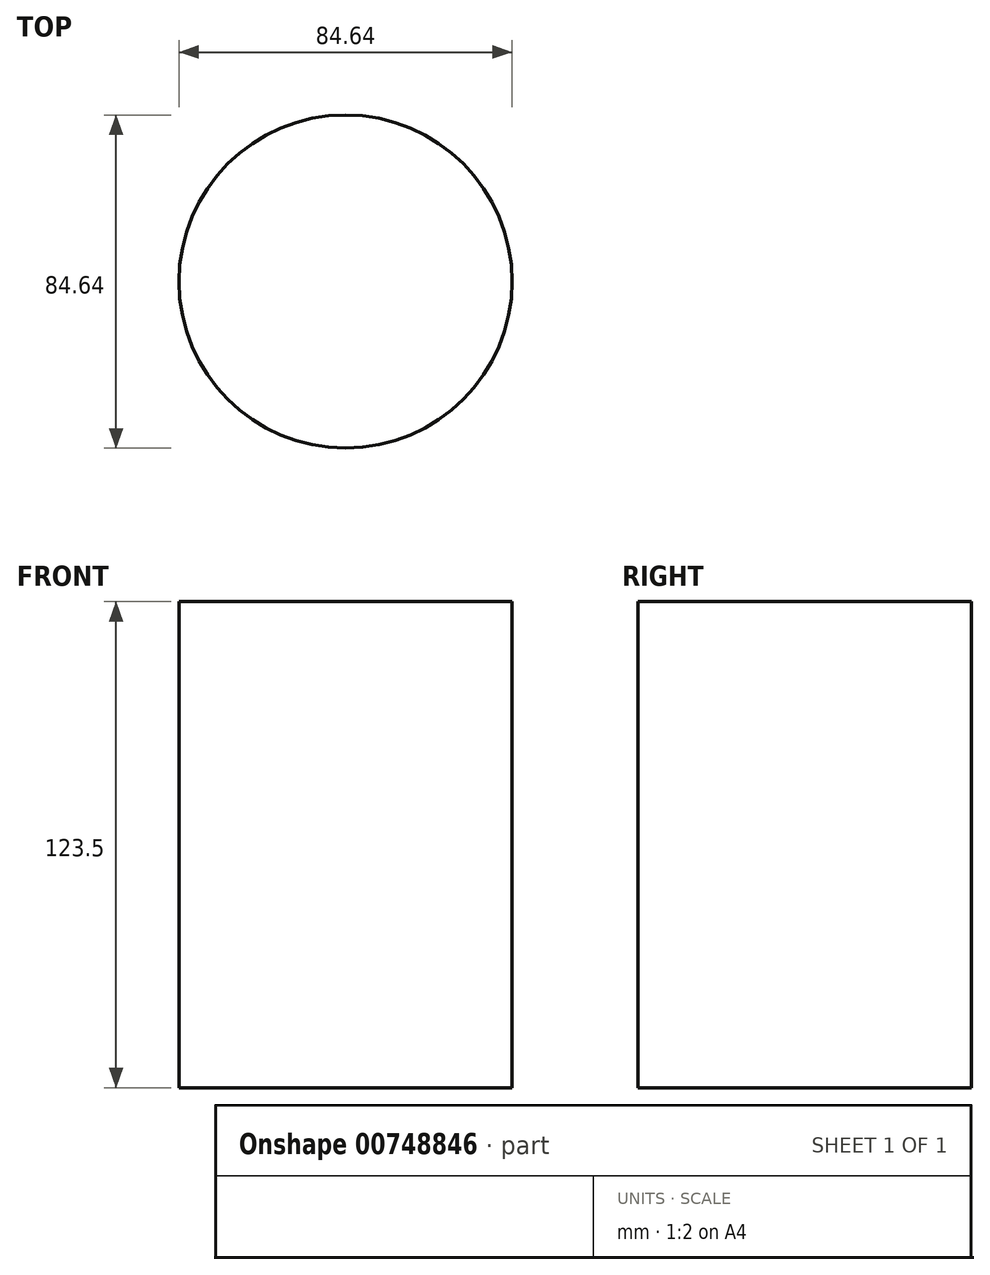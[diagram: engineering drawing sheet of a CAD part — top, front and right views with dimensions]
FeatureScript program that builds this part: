
annotation { "Feature Type Name" : "Feature", "Feature Type Description" : "" }
export const myFeature = defineFeature(function(context is Context, id is Id, definition is map)
    precondition{}
    {
        {
            var Q0;
            Q0=qCreatedBy(makeId("Top.planeOp"),FACE);
            var sketch = newSketch(context, id + "F0", { "sketchPlane" : qUnion([Q0])});
            skCircle(sketch, "E0", {"center": v(0, 0) * mm, "radius": 42.32 * mm});
            skSolve(sketch);
        }
        {
            var Q0;
            Q0 = qSketchRegion(id + "F0", true);
            extrude(context, id + "F1", {"entities" : qUnion([Q0]), "depth" : 123.5 * mm, "offsetDistance" : 25.4 * mm});
        }
    });
